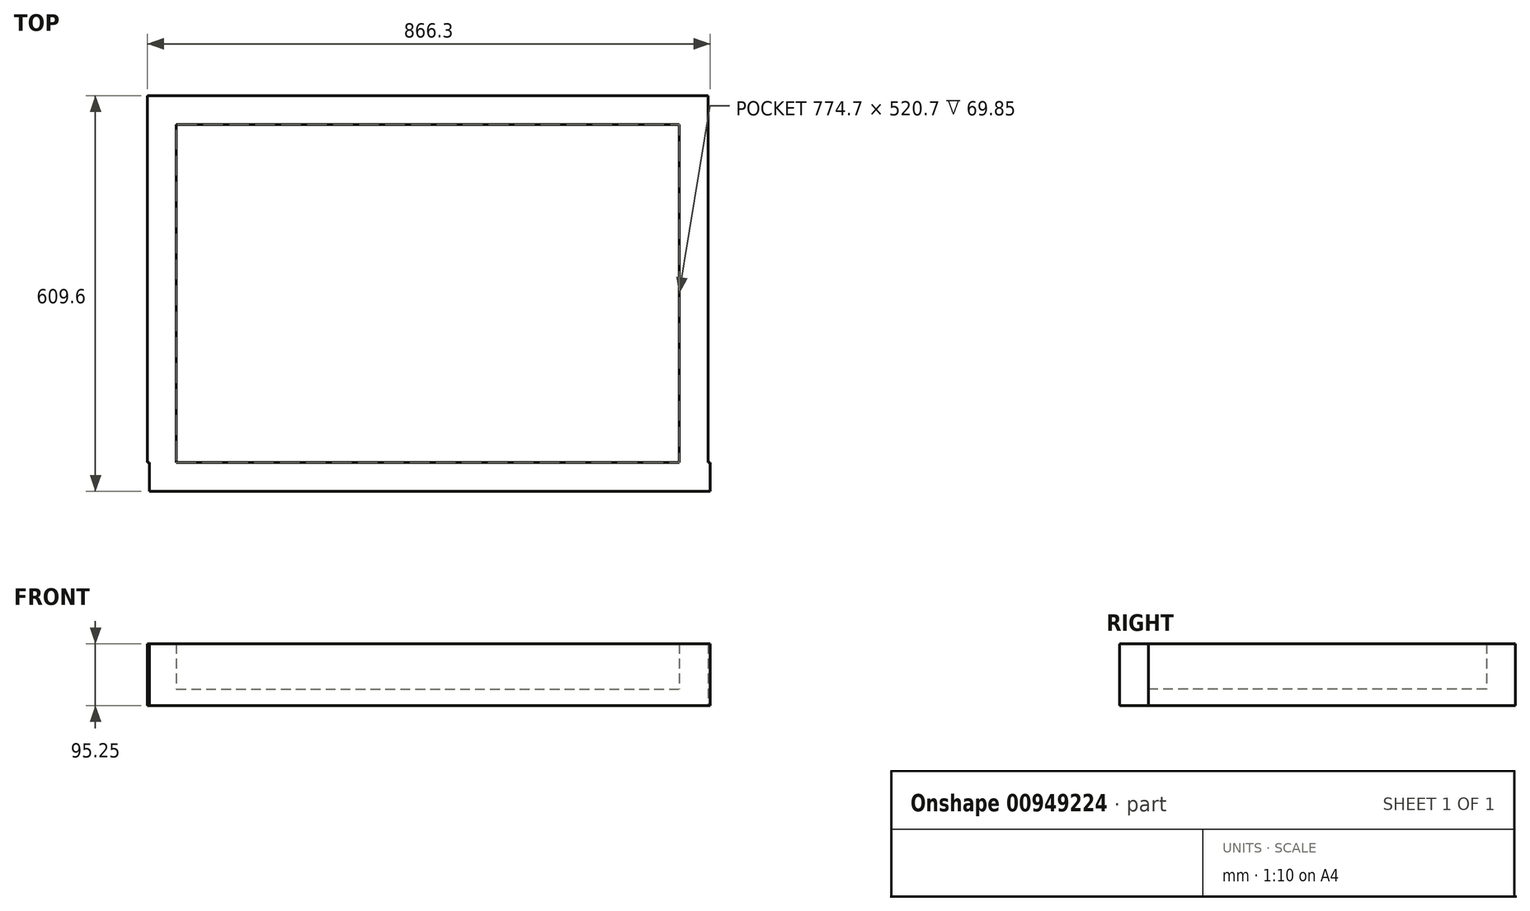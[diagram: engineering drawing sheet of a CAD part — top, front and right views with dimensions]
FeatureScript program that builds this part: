
annotation { "Feature Type Name" : "Feature", "Feature Type Description" : "" }
export const myFeature = defineFeature(function(context is Context, id is Id, definition is map)
    precondition{}
    {
        {
            var Q0;
            Q0=qCreatedBy(makeId("Top.planeOp"),FACE);
            var sketch = newSketch(context, id + "F0", { "sketchPlane" : qUnion([Q0])});
            skLineSegment(sketch, "E0.bottom", {"start": v(-432.93, 307.08) * mm, "end": v(430.67, 307.08) * mm});
            skLineSegment(sketch, "E0.top", {"start": v(-432.93, 262.63) * mm, "end": v(430.67, 262.63) * mm});
            skLineSegment(sketch, "E0.left", {"start": v(-432.93, 307.08) * mm, "end": v(-432.93, 262.63) * mm});
            skLineSegment(sketch, "E0.right", {"start": v(430.67, 307.08) * mm, "end": v(430.67, 262.63) * mm});
            skLineSegment(sketch, "E1.bottom", {"start": v(-430.23, -302.52) * mm, "end": v(433.37, -302.52) * mm});
            skLineSegment(sketch, "E1.top", {"start": v(-430.23, -258.07) * mm, "end": v(433.37, -258.07) * mm});
            skLineSegment(sketch, "E1.left", {"start": v(-430.23, -302.52) * mm, "end": v(-430.23, -258.07) * mm});
            skLineSegment(sketch, "E1.right", {"start": v(433.37, -302.52) * mm, "end": v(433.37, -258.07) * mm});
            skLineSegment(sketch, "E2.bottom", {"start": v(-432.93, 262.63) * mm, "end": v(-388.48, 262.63) * mm});
            skLineSegment(sketch, "E2.top", {"start": v(-432.93, -258.07) * mm, "end": v(-388.48, -258.07) * mm});
            skLineSegment(sketch, "E2.left", {"start": v(-432.93, 262.63) * mm, "end": v(-432.93, -258.07) * mm});
            skLineSegment(sketch, "E2.right", {"start": v(-388.48, 262.63) * mm, "end": v(-388.48, -258.07) * mm});
            skLineSegment(sketch, "E3.bottom", {"start": v(430.67, 262.63) * mm, "end": v(386.22, 262.63) * mm});
            skLineSegment(sketch, "E3.top", {"start": v(430.67, -258.07) * mm, "end": v(386.22, -258.07) * mm});
            skLineSegment(sketch, "E3.left", {"start": v(430.67, 262.63) * mm, "end": v(430.67, -258.07) * mm});
            skLineSegment(sketch, "E3.right", {"start": v(386.22, 262.63) * mm, "end": v(386.22, -258.07) * mm});
            skSolve(sketch);
        }
        {
            var Q0;
            {var subQ0=sQuery(id+"F0.wireOp",EDGE,"E3.left");Q0=makeQuery(id+"F0.imprint","IMPRINT",FACE,{"disambiguationData":[TD([[makeQuery(id+"F0.imprint","IMPRINT",EDGE,{"derivedFrom":subQ0}),-1.0]])]});}
            var Q1;
            Q1=makeQuery(id+"F0.imprint","IMPRINT",FACE,{"disambiguationData":[TD([[makeQuery(id+"F0.imprint","IMPRINT",EDGE,{"derivedFrom":sQuery(id+"F0.wireOp",EDGE,"E1.bottom")}),1.0]])]});
            var Q2;
            {var subQ4=sQuery(id+"F0.wireOp",EDGE,"E2.top");Q2=makeQuery(id+"F0.imprint","IMPRINT",FACE,{"disambiguationData":[TD([[makeQuery(id+"F0.imprint","IMPRINT",EDGE,{"derivedFrom":subQ4}),1.0]])]});}
            var Q3;
            Q3=makeQuery(id+"F0.imprint","IMPRINT",FACE,{"disambiguationData":[TD([[makeQuery(id+"F0.imprint","IMPRINT",EDGE,{"derivedFrom":sQuery(id+"F0.wireOp",EDGE,"E0.bottom")}),-1.0]])]});
            extrude(context, id + "F1", {"entities" : qUnion([Q0, Q1, Q2, Q3]), "depth" : 95.25 * mm, "offsetDistance" : 25.4 * mm});
        }
        {
            var Q0;
            {var subQ0=sQuery(id+"F0.wireOp",EDGE,"E2.right");Q0=makeQuery(id+"F0.imprint","IMPRINT",FACE,{"disambiguationData":[TD([[makeQuery(id+"F0.imprint","IMPRINT",EDGE,{"derivedFrom":subQ0}),1.0]])]});}
            extrude(context, id + "F2", {"entities" : qUnion([Q0]), "operationType" : NewBodyOperationType.ADD, "depth" : 25.4 * mm, "offsetDistance" : 25.4 * mm});
        }
    });
